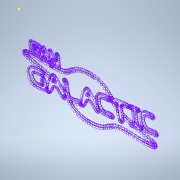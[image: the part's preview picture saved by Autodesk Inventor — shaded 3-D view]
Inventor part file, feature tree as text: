
AUTODESK INVENTOR PART (.ipt)
format: ipt  version: 2022 (Build 260153000, 153)  size: 476,160 bytes
history: native  units: in
note: dims shown in document units (in); Inventor stores cm internally (conversion verified against a paired STEP export)
features: sketch x1
ambient origin geometry x8: Origin, YZ Plane, XZ Plane, XY Plane, X Axis, Y Axis, Z Axis, Center Point
feature tree (1):
  sketch  "Sketch1"
